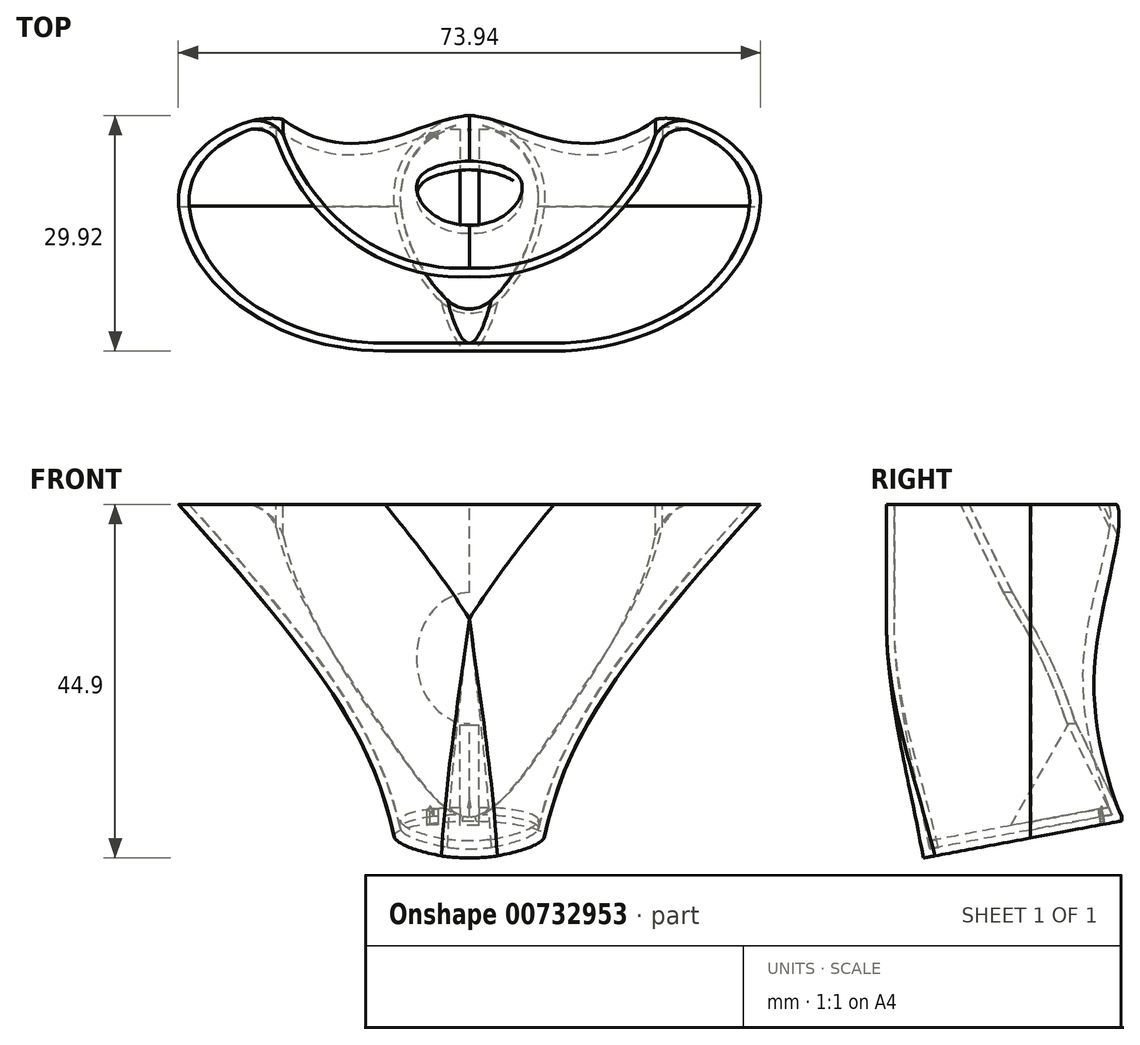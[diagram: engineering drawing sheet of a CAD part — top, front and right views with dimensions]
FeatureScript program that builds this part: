
annotation { "Feature Type Name" : "Feature", "Feature Type Description" : "" }
export const myFeature = defineFeature(function(context is Context, id is Id, definition is map)
    precondition{}
    {
        {
            var Q0;
            Q0=qCreatedBy(makeId("Front.planeOp"),FACE);
            var sketch = newSketch(context, id + "F0", { "sketchPlane" : qUnion([Q0])});
            skLineSegment(sketch, "E0", {"start": v(-9, -21.86) * mm, "end": v(9, -21.86) * mm});
            skLineSegment(sketch, "E1", {"start": v(0, -21.86) * mm, "end": v(0, 23.14) * mm, "construction": true});
            skLineSegment(sketch, "E2", {"start": v(-37, 23.14) * mm, "end": v(37, 23.14) * mm});
            skFitSpline(sketch, "E3", {"points": [v(-37, 23.14) * mm, v(-9, -21.86) * mm], "startDerivative": vector(66.87, -73.39) * mm, "endDerivative": vector(7.33, -37.29) * mm});
            skFitSpline(sketch, "E4.MirrorCS", {"points": [v(37, 23.14) * mm, v(9, -21.86) * mm], "startDerivative": vector(-66.87, -73.39) * mm, "endDerivative": vector(-7.33, -37.29) * mm});
            skSolve(sketch);
        }
        {
            var Q0;
            Q0=makeQuery(id+"F0.imprint","IMPRINT",FACE,{"disambiguationData":[TD([[makeQuery(id+"F0.imprint","IMPRINT",EDGE,{"derivedFrom":sQuery(id+"F0.wireOp",EDGE,"E0")}),1.0]])]});
            extrude(context, id + "F1", {"entities" : qUnion([Q0]), "depth" : 30 * mm, "offsetDistance" : 25 * mm});
        }
        {
            var Q0;
            Q0=makeQuery(id+"F1.opExtrude","CAP_EDGE",EDGE,{"disambiguationData":[OSD([sQuery(id+"F0.wireOp",EDGE,"E3")])],"isStart":false});
            var Q1;
            Q1=makeQuery(id+"F1.opExtrude","CAP_EDGE",EDGE,{"disambiguationData":[OSD([sQuery(id+"F0.wireOp",EDGE,"E4.MirrorCS")])],"isStart":false});
            fillet(context, id + "F2", {"entities" : qUnion([Q0, Q1]), "radius" : 19.8 * mm, "tangentPropagation" : true, "allowEdgeOverflow" : false});
        }
        {
            var Q0;
            Q0=makeQuery(id+"F1.opExtrude","CAP_EDGE",EDGE,{"disambiguationData":[OSD([sQuery(id+"F0.wireOp",EDGE,"E3")])],"isStart":true});
            var Q1;
            Q1=makeQuery(id+"F1.opExtrude","CAP_EDGE",EDGE,{"disambiguationData":[OSD([sQuery(id+"F0.wireOp",EDGE,"E4.MirrorCS")])],"isStart":true});
            fillet(context, id + "F3", {"entities" : qUnion([Q0, Q1]), "radius" : 10.86 * mm, "tangentPropagation" : true, "allowEdgeOverflow" : false});
        }
        {
            var Q0;
            Q0=makeQuery(id+"F2.opFillet","BLEND_EDGE",EDGE,{"blendedFrom":[makeQuery(id+"F1.opExtrude","CAP_EDGE",EDGE,{"disambiguationData":[OSD([sQuery(id+"F0.wireOp",EDGE,"E3")])],"isStart":false}),makeQuery(id+"F1.opExtrude","CAP_EDGE",EDGE,{"disambiguationData":[OSD([sQuery(id+"F0.wireOp",EDGE,"E4.MirrorCS")])],"isStart":false})],"blendedInto":[]});
            fillet(context, id + "F4", {"entities" : qUnion([Q0]), "radius" : 5 * mm, "tangentPropagation" : true, "allowEdgeOverflow" : false});
        }
        {
            var Q0;
            Q0=makeQuery(id+"F3.opFillet","BLEND_EDGE",EDGE,{"blendedFrom":[makeQuery(id+"F1.opExtrude","CAP_EDGE",EDGE,{"disambiguationData":[OSD([sQuery(id+"F0.wireOp",EDGE,"E3")])],"isStart":true}),makeQuery(id+"F1.opExtrude","CAP_EDGE",EDGE,{"disambiguationData":[OSD([sQuery(id+"F0.wireOp",EDGE,"E4.MirrorCS")])],"isStart":true})],"blendedInto":[]});
            fillet(context, id + "F5", {"entities" : qUnion([Q0]), "radius" : 5 * mm, "tangentPropagation" : true, "allowEdgeOverflow" : false});
        }
        {
            var Q0;
            Q0=qCreatedBy(makeId("Right.planeOp"),FACE);
            var sketch = newSketch(context, id + "F6", { "sketchPlane" : qUnion([Q0])});
            skLineSegment(sketch, "E5", {"start": v(-31.86, -23) * mm, "end": v(8.16, -15.5) * mm});
            skLineSegment(sketch, "E6", {"start": v(8.16, -15.5) * mm, "end": v(3.01, -25.08) * mm});
            skLineSegment(sketch, "E7", {"start": v(3.01, -25.08) * mm, "end": v(-31.86, -23) * mm});
            skSolve(sketch);
        }
        {
            var Q0;
            Q0=qSketchRegion(id+"F6",true);
            extrude(context, id + "F7", {"entities" : qUnion([Q0]), "operationType" : NewBodyOperationType.REMOVE, "depth" : 25 * mm, "offsetDistance" : 25 * mm, "hasSecondDirection" : true, "secondDirectionOppositeDirection" : true, "secondDirectionDepth" : 25 * mm});
        }
        {
            var Q0;
            Q0=qCreatedBy(makeId("Right.planeOp"),FACE);
            var sketch = newSketch(context, id + "F8", { "sketchPlane" : qUnion([Q0])});
            skLineSegment(sketch, "E8", {"start": v(-24.08, 32.66) * mm, "end": v(0, 44.42) * mm});
            skSolve(sketch);
        }
        {
            var Q0;
            Q0=sQuery(id+"F8.wireOp",EDGE,"E8");
            extrude(context, id + "F9", {"bodyType" : ToolBodyType.SURFACE, "surfaceEntities" : qUnion([Q0]), "depth" : 25 * mm, "offsetDistance" : 25 * mm, "hasSecondDirection" : true, "secondDirectionOppositeDirection" : true, "secondDirectionDepth" : 25 * mm});
        }
        {
            var Q0;
            Q0=makeQuery(id+"F9.opExtrude","SWEPT_FACE",FACE,{"disambiguationData":[OSD([sQuery(id+"F8.wireOp",EDGE,"E8")])]});
            var sketch = newSketch(context, id + "F10", { "sketchPlane" : qUnion([Q0])});
            skArc(sketch, "E9", {"start": v(23.67, -7.9) * mm, "mid": v(14.28, 3.52) * mm, "end": v(0, 7.3) * mm});
            skFitSpline(sketch, "E10", {"points": [v(23.67, -7.9) * mm, v(31.63, -8.58) * mm], "startDerivative": vector(3.77, -5) * mm, "endDerivative": vector(13, 4.88) * mm});
            skLineSegment(sketch, "E11", {"start": v(31.63, -8.58) * mm, "end": v(10.84, -28.18) * mm});
            skLineSegment(sketch, "E12", {"start": v(10.84, -28.18) * mm, "end": v(0, -18.9) * mm});
            skLineSegment(sketch, "E13", {"start": v(0, 4.27) * mm, "end": v(0, -45.58) * mm, "construction": true});
            skFitSpline(sketch, "E14.MirrorCS", {"points": [v(-23.67, -7.9) * mm, v(-31.63, -8.58) * mm], "startDerivative": vector(-3.77, -5) * mm, "endDerivative": vector(-13, 4.88) * mm});
            skLineSegment(sketch, "E15.MirrorCS", {"start": v(-31.63, -8.58) * mm, "end": v(-10.84, -28.18) * mm});
            skLineSegment(sketch, "E16.MirrorCS", {"start": v(-10.84, -28.18) * mm, "end": v(0, -18.9) * mm});
            skArc(sketch, "E17.MirrorCS", {"start": v(-23.67, -7.9) * mm, "mid": v(-14.28, 3.52) * mm, "end": v(0, 7.3) * mm});
            skPoint(sketch, "E18.orphan", {"position": v(-24.25, -9.56) * mm});
            skPoint(sketch, "E19.orphan", {"position": v(24.25, -9.56) * mm});
            skSolve(sketch);
        }
        {
            var Q0;
            Q0=qSketchRegion(id+"F10",true);
            extrude(context, id + "F11", {"entities" : qUnion([Q0]), "operationType" : NewBodyOperationType.REMOVE, "depth" : 77.2 * mm, "offsetDistance" : 25 * mm});
        }
        {
            var Q0;
            Q0=makeQuery(id+"F9.opExtrude","SWEPT_BODY",BODY,{"disambiguationData":[OSD([sQuery(id+"F8.wireOp",EDGE,"E8")])]});
            deleteBodies(context, id + "F12", {"entities" : qUnion([Q0])});
        }
        {
            var Q0;
            Q0=makeQuery(id+"F1.opExtrude","SWEPT_FACE",FACE,{"disambiguationData":[OSD([sQuery(id+"F0.wireOp",EDGE,"E2")])]});
            shell(context, id + "F13", {"entities" : qUnion([Q0]), "thickness" : 1 * mm});
        }
        {
            var Q0;
            Q0=makeQuery(id+"F7.boolean.opBoolean","COPY",FACE,{"derivedFrom":makeQuery(id+"F7.opExtrude","SWEPT_FACE",FACE,{"disambiguationData":[OSD([sQuery(id+"F6.wireOp",EDGE,"E5")])]})});
            var sketch = newSketch(context, id + "F14", { "sketchPlane" : qUnion([Q0])});
            skFitSpline(sketch, "E20", {"points": [v(-5.51, 5.37) * mm, v(-4, 5.85) * mm, v(-3.4, 8.02) * mm, v(-5.7, 12.02) * mm, v(-4.58, 21.11) * mm, v(0, 25.37) * mm], "startDerivative": vector(11.33, -0.98) * mm, "endDerivative": vector(15.89, -0.05) * mm});
            skFitSpline(sketch, "E21.MirrorCS", {"points": [v(5.51, 5.37) * mm, v(4, 5.85) * mm, v(3.4, 8.02) * mm, v(5.7, 12.02) * mm, v(4.58, 21.11) * mm, v(0, 25.37) * mm], "startDerivative": vector(-11.33, -0.98) * mm, "endDerivative": vector(-15.89, -0.05) * mm});
            skFitSpline(sketch, "E22", {"points": [v(0, 27.88) * mm, v(-2.51, 27.15) * mm, v(-6.1, 22.7) * mm, v(-7.89, 18.78) * mm, v(-8.68, 15.18) * mm, v(-8.46, 11.07) * mm, v(-6.69, 7.46) * mm, v(-4.98, 5.4) * mm], "startDerivative": vector(-23.61, -0.54) * mm, "endDerivative": vector(20.39, -26.15) * mm});
            skArc(sketch, "E23.filletArc", {"start": v(-5.43, 5.96) * mm, "mid": v(-4.73, 5.6) * mm, "end": v(-3.99, 5.85) * mm});
            skFitSpline(sketch, "E24.MirrorCS", {"points": [v(0, 27.88) * mm, v(2.51, 27.15) * mm, v(6.1, 22.7) * mm, v(7.89, 18.78) * mm, v(8.68, 15.18) * mm, v(8.46, 11.07) * mm, v(6.69, 7.46) * mm, v(4.98, 5.4) * mm], "startDerivative": vector(23.61, -0.54) * mm, "endDerivative": vector(-20.39, -26.15) * mm});
            skArc(sketch, "E25.MirrorCS", {"start": v(5.43, 5.96) * mm, "mid": v(4.73, 5.6) * mm, "end": v(3.99, 5.85) * mm});
            skSolve(sketch);
        }
        {
            var Q0;
            Q0=makeQuery(id+"F14.imprint","IMPRINT",FACE,{"disambiguationData":[TD([[makeQuery(id+"F14.imprint","IMPRINT",EDGE,{"derivedFrom":sQuery(id+"F14.wireOp",EDGE,"E20")}),1.0]])]});
            extrude(context, id + "F15", {"entities" : qUnion([Q0]), "operationType" : NewBodyOperationType.REMOVE, "oppositeDirection" : true, "depth" : 3 * mm, "offsetDistance" : 25 * mm});
        }
        {
            var Q0;
            Q0=qCreatedBy(makeId("Right.planeOp"),FACE);
            var sketch = newSketch(context, id + "F16", { "sketchPlane" : qUnion([Q0])});
            skLineSegment(sketch, "E26", {"start": v(-14.52, -18.2) * mm, "end": v(-6.85, -4.74) * mm});
            skLineSegment(sketch, "E27", {"start": v(-6.85, -4.74) * mm, "end": v(-1.66, -15.56) * mm});
            skLineSegment(sketch, "E28", {"start": v(-1.66, -15.56) * mm, "end": v(-14.52, -18.2) * mm});
            skSolve(sketch);
        }
        {
            var Q0;
            Q0=qSketchRegion(id+"F16",true);
            extrude(context, id + "F17", {"entities" : qUnion([Q0]), "operationType" : NewBodyOperationType.ADD, "depth" : 1.2 * mm, "offsetDistance" : 25 * mm, "hasSecondDirection" : true, "secondDirectionOppositeDirection" : true, "secondDirectionDepth" : 1.2 * mm});
        }
        {
            var Q0;
            Q0=makeQuery(id+"F14.imprint","IMPRINT",FACE,{"disambiguationData":[TD([[makeQuery(id+"F14.imprint","IMPRINT",EDGE,{"derivedFrom":sQuery(id+"F14.wireOp",EDGE,"E20")}),1.0]])]});
            extrude(context, id + "F18", {"entities" : qUnion([Q0]), "operationType" : NewBodyOperationType.REMOVE, "oppositeDirection" : true, "depth" : 3 * mm, "offsetDistance" : 25 * mm});
        }
        {
            var Q0;
            Q0=qCreatedBy(makeId("Front.planeOp"),FACE);
            var sketch = newSketch(context, id + "F19", { "sketchPlane" : qUnion([Q0])});
            skLineSegment(sketch, "E29.left", {"start": v(11, 3.63) * mm, "end": v(11, 3.63) * mm});
            skLineSegment(sketch, "E29.right", {"start": v(-11, 3.63) * mm, "end": v(-11, 3.63) * mm});
            skPoint(sketch, "E29.middle", {"position": v(0, 3.63) * mm});
            skPoint(sketch, "E30.visualSharp", {"position": v(11, 5.13) * mm});
            skPoint(sketch, "E31.visualSharp", {"position": v(11, 2.13) * mm});
            skPoint(sketch, "E32.visualSharp", {"position": v(-11, 5.13) * mm});
            skPoint(sketch, "E33.visualSharp", {"position": v(-11, 2.13) * mm});
            skEllipse(sketch, "E34", {"center": v(0, 3.63) * mm, "majorRadius": 8.32 * mm, "minorRadius": 6.72 * mm, "majorAxis": v(0, -1)});
            skSolve(sketch);
        }
        {
            var Q0;
            Q0=qSketchRegion(id+"F19",true);
            extrude(context, id + "F20", {"entities" : qUnion([Q0]), "operationType" : NewBodyOperationType.REMOVE, "depth" : 17.8 * mm, "offsetDistance" : 25 * mm});
        }
        {
            var Q0;
            Q0=makeQuery(id+"F15.boolean.opBoolean","SPLIT",FACE,{"disambiguationData":[TD([makeQuery(id+"F13.opShell","OFFSET_FACE",FACE,{"disambiguationData":[OSD([sQuery(id+"F10.wireOp",EDGE,"E9")])]})])],"derivedFrom":makeQuery(id+"F13.opShell","OFFSET_FACE",FACE,{"disambiguationData":[OSD([sQuery(id+"F6.wireOp",EDGE,"E5")])]})});
            extrude(context, id + "F21", {"entities" : qUnion([Q0]), "operationType" : NewBodyOperationType.ADD, "depth" : 1 * mm, "offsetDistance" : 25 * mm});
        }
    });
